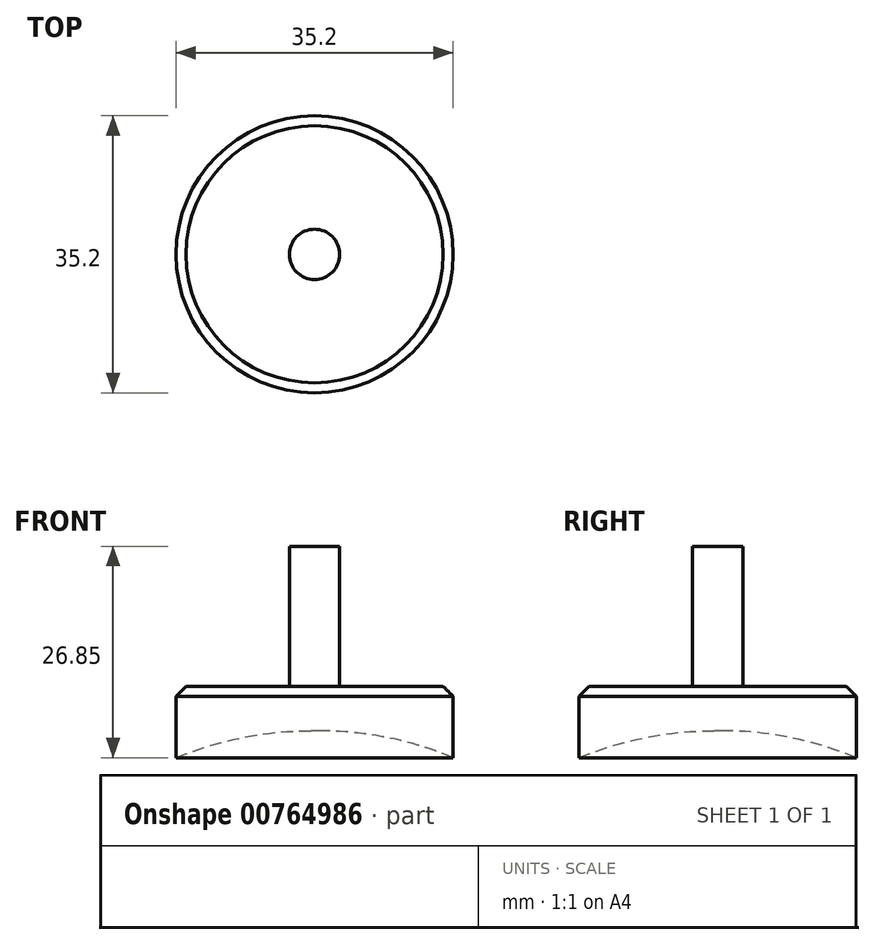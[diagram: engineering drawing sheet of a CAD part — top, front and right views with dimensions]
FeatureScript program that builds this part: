
annotation { "Feature Type Name" : "Feature", "Feature Type Description" : "" }
export const myFeature = defineFeature(function(context is Context, id is Id, definition is map)
    precondition{}
    {
        {
            var Q0;
            Q0=qCreatedBy(makeId("Front.planeOp"),FACE);
            var sketch = newSketch(context, id + "F0", { "sketchPlane" : qUnion([Q0])});
            skLineSegment(sketch, "E0", {"start": v(0, 45.15) * mm, "end": v(0, -44.31) * mm});
            skArc(sketch, "E1", {"start": v(0, -44.31) * mm, "mid": v(45.16, 0.42) * mm, "end": v(0, 45.15) * mm});
            skSolve(sketch);
        }
        {
            var Q0;
            Q0=makeQuery(id+"F0.imprint","IMPRINT",FACE,{"disambiguationData":[TD([[makeQuery(id+"F0.imprint","IMPRINT",EDGE,{"derivedFrom":sQuery(id+"F0.wireOp",EDGE,"E0")}),1.0]])]});
            var Q1;
            Q1=sQuery(id+"F0.wireOp",EDGE,"E0");
            revolve(context, id + "F1", {"surfaceOperationType" : NewSurfaceOperationType.NEW, "entities" : qUnion([Q0]), "axis" : qUnion([Q1]), "revolveType" : RevolveType.FULL});
        }
        {
            var Q0;
            Q0=qCreatedBy(makeId("Top.planeOp"),FACE);
            var sketch = newSketch(context, id + "F2", { "sketchPlane" : qUnion([Q0])});
            skCircle(sketch, "E2", {"center": v(0, 0) * mm, "radius": 17.6 * mm});
            skSolve(sketch);
        }
        {
            var Q0;
            Q0 = qSketchRegion(id + "F2", true);
            extrude(context, id + "F3", {"entities" : qUnion([Q0]), "operationType" : NewBodyOperationType.ADD, "depth" : 50.8 * mm, "offsetDistance" : 25.4 * mm});
        }
        {
            var Q0;
            Q0=makeQuery(id+"F3.opExtrude","CAP_EDGE",EDGE,{"disambiguationData":[OSD([sQuery(id+"F2.wireOp",EDGE,"E2")])],"isStart":false});
            chamfer(context, id + "F4", {"entities" : qUnion([Q0]), "width" : 1.27 * mm, "tangentPropagation" : true});
        }
        {
            var Q0;
            Q0=qCreatedBy(makeId("Top.planeOp"),FACE);
            var sketch = newSketch(context, id + "F5", { "sketchPlane" : qUnion([Q0])});
            skCircle(sketch, "E3", {"center": v(0, 0) * mm, "radius": 3.2 * mm});
            skSolve(sketch);
        }
        {
            var Q0;
            Q0 = qSketchRegion(id + "F5", true);
            extrude(context, id + "F6", {"entities" : qUnion([Q0]), "operationType" : NewBodyOperationType.ADD, "depth" : 68.58 * mm, "offsetDistance" : 25.4 * mm});
        }
        {
            var Q0;
            Q0=qCreatedBy(makeId("Top.planeOp"),FACE);
            var sketch = newSketch(context, id + "F7", { "sketchPlane" : qUnion([Q0])});
            skCircle(sketch, "E4", {"center": v(-21.76, 5.85) * mm, "radius": 5.85 * mm});
            skCircle(sketch, "E5", {"center": v(21.76, 5.85) * mm, "radius": 6.16 * mm});
            skSolve(sketch);
        }
        {
            var Q0;
            Q0 = qSketchRegion(id + "F7", true);
            extrude(context, id + "F8", {"entities" : qUnion([Q0]), "operationType" : NewBodyOperationType.ADD, "oppositeDirection" : true, "depth" : 64.77 * mm, "offsetDistance" : 25.4 * mm});
        }
        {
            var Q0;
            Q0=makeQuery(id+"F8.opExtrude","CAP_FACE",FACE,{"disambiguationData":[OSD([sQuery(id+"F7.wireOp",EDGE,"E4")])],"isStart":false});
            var sketch = newSketch(context, id + "F9", { "sketchPlane" : qUnion([Q0])});
            skArc(sketch, "E6", {"start": v(32.74, 17.17) * mm, "mid": v(22.04, 38.7) * mm, "end": v(10.88, 17.4) * mm});
            skLineSegment(sketch, "E7", {"start": v(32.74, 17.17) * mm, "end": v(28.32, -7.02) * mm});
            skArc(sketch, "E8", {"start": v(15.3, -7.02) * mm, "mid": v(21.81, -12.45) * mm, "end": v(28.32, -7.02) * mm});
            skLineSegment(sketch, "E9", {"start": v(15.3, -7.02) * mm, "end": v(10.88, 17.4) * mm});
            skArc(sketch, "E10", {"start": v(-10.87, 17.17) * mm, "mid": v(-21.57, 38.7) * mm, "end": v(-32.73, 17.4) * mm});
            skLineSegment(sketch, "E11", {"start": v(-10.87, 17.17) * mm, "end": v(-15.29, -7.02) * mm});
            skArc(sketch, "E12", {"start": v(-28.31, -7.02) * mm, "mid": v(-21.8, -12.45) * mm, "end": v(-15.29, -7.02) * mm});
            skLineSegment(sketch, "E13", {"start": v(-28.31, -7.02) * mm, "end": v(-32.73, 17.4) * mm});
            skSolve(sketch);
        }
        {
            var Q0;
            Q0 = qSketchRegion(id + "F9", true);
            extrude(context, id + "F10", {"entities" : qUnion([Q0]), "operationType" : NewBodyOperationType.ADD, "oppositeDirection" : true, "depth" : 12.7 * mm, "offsetDistance" : 25.4 * mm});
        }
        {
            var Q0;
            Q0=qCreatedBy(makeId("Front.planeOp"),FACE);
            var sketch = newSketch(context, id + "F11", { "sketchPlane" : qUnion([Q0])});
            skEllipse(sketch, "E14", {"center": v(-19.8, 0.05) * mm, "majorRadius": 21.93 * mm, "minorRadius": 4.94 * mm, "majorAxis": v(0, -1)});
            skEllipse(sketch, "E15", {"center": v(18.33, 0.1) * mm, "majorRadius": 21.93 * mm, "minorRadius": 4.94 * mm, "majorAxis": v(0, -1)});
            skSolve(sketch);
        }
        {
            var Q0;
            Q0 = qSketchRegion(id + "F11", true);
            extrude(context, id + "F12", {"entities" : qUnion([Q0]), "operationType" : NewBodyOperationType.ADD, "depth" : 43.18 * mm, "offsetDistance" : 25.4 * mm});
        }
    });
